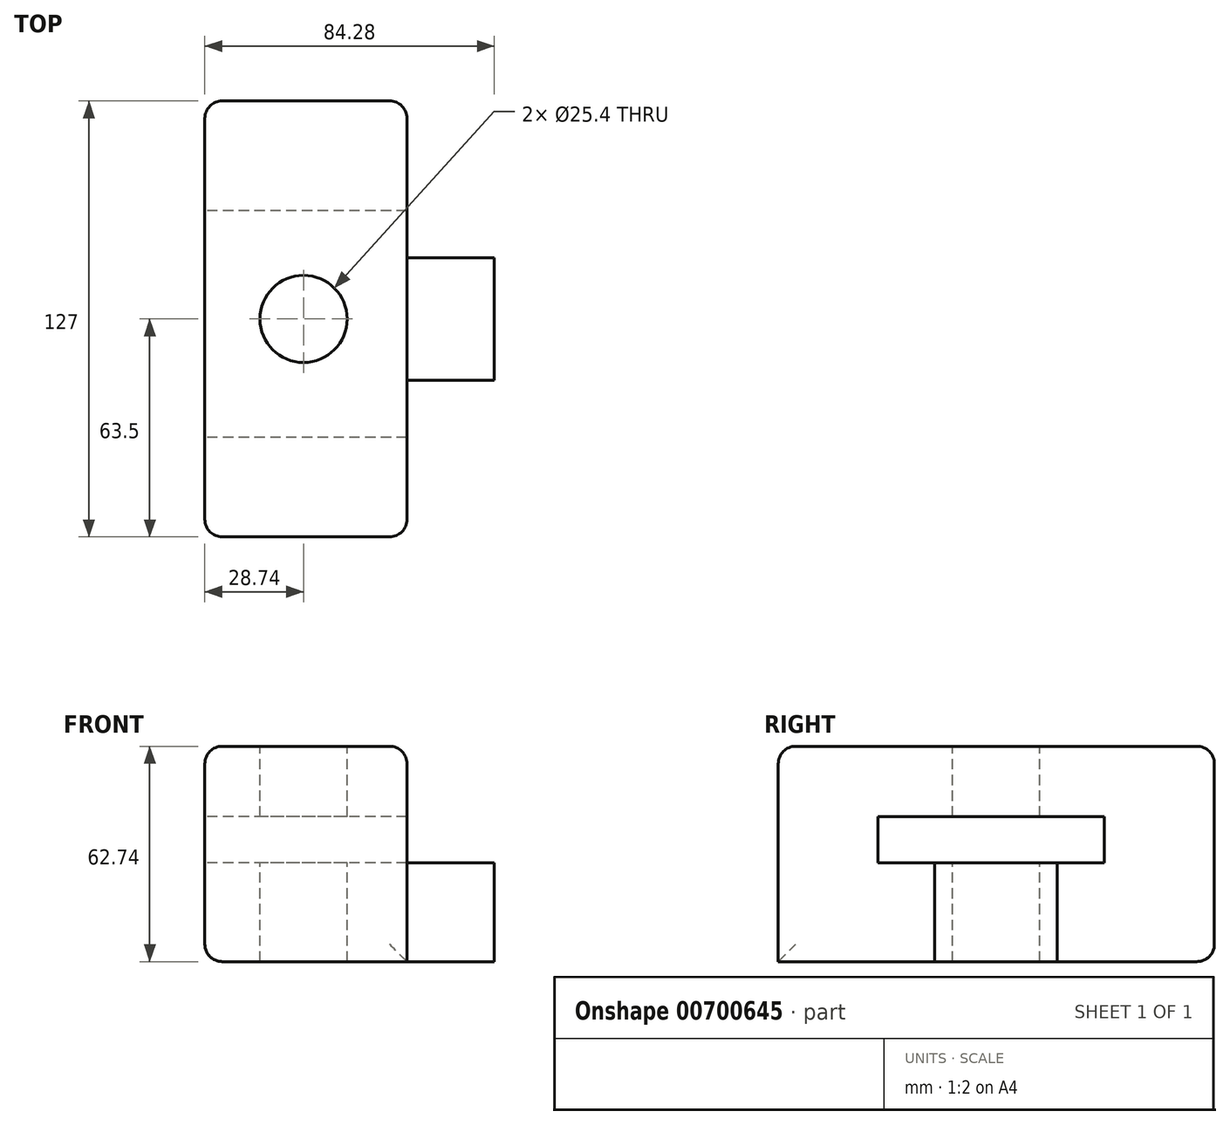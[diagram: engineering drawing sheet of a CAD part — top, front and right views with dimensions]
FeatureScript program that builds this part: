
annotation { "Feature Type Name" : "Feature", "Feature Type Description" : "" }
export const myFeature = defineFeature(function(context is Context, id is Id, definition is map)
    precondition{}
    {
        {
            var Q0;
            Q0=qCreatedBy(makeId("Front.planeOp"),FACE);
            var sketch = newSketch(context, id + "F0", { "sketchPlane" : qUnion([Q0])});
            skLineSegment(sketch, "E0.bottom", {"start": v(-28.74, 34) * mm, "end": v(30.14, 34) * mm});
            skLineSegment(sketch, "E0.top", {"start": v(-28.74, -28.73) * mm, "end": v(30.14, -28.73) * mm});
            skLineSegment(sketch, "E0.left", {"start": v(-28.74, 34) * mm, "end": v(-28.74, -28.73) * mm});
            skLineSegment(sketch, "E0.right", {"start": v(30.14, 34) * mm, "end": v(30.14, -28.73) * mm});
            skSolve(sketch);
        }
        {
            var Q0;
            Q0=makeQuery(id+"F0.imprint","IMPRINT",FACE,{"disambiguationData":[TD([[makeQuery(id+"F0.imprint","IMPRINT",EDGE,{"derivedFrom":sQuery(id+"F0.wireOp",EDGE,"E0.bottom")}),-1.0]])]});
            extrude(context, id + "F1", {"entities" : qUnion([Q0]), "endBound" : BoundingType.SYMMETRIC, "depth" : 127 * mm, "offsetDistance" : 25.4 * mm});
        }
        {
            var Q0;
            Q0=qCreatedBy(makeId("Right.planeOp"),FACE);
            var sketch = newSketch(context, id + "F2", { "sketchPlane" : qUnion([Q0])});
            skLineSegment(sketch, "E1.bottom", {"start": v(-34.45, 13.5) * mm, "end": v(31.48, 13.5) * mm});
            skLineSegment(sketch, "E1.top", {"start": v(-34.45, 0) * mm, "end": v(31.48, 0) * mm});
            skLineSegment(sketch, "E1.left", {"start": v(-34.45, 13.5) * mm, "end": v(-34.45, 0) * mm});
            skLineSegment(sketch, "E1.right", {"start": v(31.48, 13.5) * mm, "end": v(31.48, 0) * mm});
            skSolve(sketch);
        }
        {
            var Q0;
            Q0 = qSketchRegion(id + "F2", true);
            extrude(context, id + "F3", {"entities" : qUnion([Q0]), "operationType" : NewBodyOperationType.REMOVE, "endBound" : BoundingType.THROUGH_ALL, "depth" : 25.4 * mm, "offsetDistance" : 25.4 * mm, "hasSecondDirection" : true, "secondDirectionBound" : SecondDirectionBoundingType.UP_TO_NEXT, "secondDirectionOppositeDirection" : true, "secondDirectionDepth" : 25.4 * mm});
        }
        {
            var Q0;
            Q0=makeQuery(id+"F1.opExtrude","CAP_EDGE",EDGE,{"disambiguationData":[OSD([sQuery(id+"F0.wireOp",EDGE,"E0.bottom")])],"isStart":true});
            fillet(context, id + "F4", {"entities" : qUnion([Q0]), "radius" : 5.08 * mm, "tangentPropagation" : true, "allowEdgeOverflow" : false});
        }
        {
            var Q0;
            Q0=makeQuery(id+"F1.opExtrude","CAP_EDGE",EDGE,{"disambiguationData":[OSD([sQuery(id+"F0.wireOp",EDGE,"E0.bottom")])],"isStart":false});
            fillet(context, id + "F5", {"entities" : qUnion([Q0]), "radius" : 5.08 * mm, "tangentPropagation" : true, "allowEdgeOverflow" : false});
        }
        {
            var Q0;
            Q0=makeQuery(id+"F1.opExtrude","SWEPT_EDGE",EDGE,{"disambiguationData":[OSD([sQuery(id+"F0.wireOp",EDGE,"E0.top"),sQuery(id+"F0.wireOp",EDGE,"E0.left")])]});
            var Q1;
            Q1=makeQuery(id+"F1.opExtrude","CAP_EDGE",EDGE,{"disambiguationData":[OSD([sQuery(id+"F0.wireOp",EDGE,"E0.left")])],"isStart":false});
            var Q2;
            Q2=makeQuery(id+"F1.opExtrude","CAP_EDGE",EDGE,{"disambiguationData":[OSD([sQuery(id+"F0.wireOp",EDGE,"E0.left")])],"isStart":true});
            var Q3;
            Q3=makeQuery(id+"F1.opExtrude","CAP_EDGE",EDGE,{"disambiguationData":[OSD([sQuery(id+"F0.wireOp",EDGE,"E0.right")])],"isStart":true});
            var Q4;
            Q4=makeQuery(id+"F1.opExtrude","SWEPT_EDGE",EDGE,{"disambiguationData":[OSD([sQuery(id+"F0.wireOp",EDGE,"E0.bottom"),sQuery(id+"F0.wireOp",EDGE,"E0.right")])]});
            var Q5;
            Q5=makeQuery(id+"F1.opExtrude","SWEPT_EDGE",EDGE,{"disambiguationData":[OSD([sQuery(id+"F0.wireOp",EDGE,"E0.bottom"),sQuery(id+"F0.wireOp",EDGE,"E0.left")])]});
            var Q6;
            Q6=makeQuery(id+"F1.opExtrude","CAP_EDGE",EDGE,{"disambiguationData":[OSD([sQuery(id+"F0.wireOp",EDGE,"E0.top")])],"isStart":true});
            fillet(context, id + "F6", {"entities" : qUnion([Q0, Q1, Q2, Q3, Q4, Q5, Q6]), "radius" : 5.08 * mm, "tangentPropagation" : true, "allowEdgeOverflow" : false});
        }
        {
            var Q0;
            Q0=makeQuery(id+"F1.opExtrude","SWEPT_FACE",FACE,{"disambiguationData":[OSD([sQuery(id+"F0.wireOp",EDGE,"E0.right")])]});
            var sketch = newSketch(context, id + "F7", { "sketchPlane" : qUnion([Q0])});
            skLineSegment(sketch, "E2", {"start": v(-17.92, 0) * mm, "end": v(-17.92, -28.73) * mm});
            skLineSegment(sketch, "E3", {"start": v(17.76, 0) * mm, "end": v(17.76, -28.73) * mm});
            skSolve(sketch);
        }
        {
            var Q0;
            {var subQ0=sQuery(id+"F7.wireOp",EDGE,"E2");Q0=makeQuery(id+"F7.imprint","IMPRINT",FACE,{"disambiguationData":[TD([[makeQuery(id+"F7.imprint","IMPRINT",EDGE,{"derivedFrom":subQ0}),1.0]])]});}
            extrude(context, id + "F8", {"entities" : qUnion([Q0]), "operationType" : NewBodyOperationType.ADD, "depth" : 25.4 * mm, "offsetDistance" : 25.4 * mm});
        }
        {
            var Q0;
            Q0=makeQuery(id+"F1.opExtrude","SWEPT_FACE",FACE,{"disambiguationData":[OSD([sQuery(id+"F0.wireOp",EDGE,"E0.bottom")])]});
            var sketch = newSketch(context, id + "F9", { "sketchPlane" : qUnion([Q0])});
            skPoint(sketch, "E4", {"position": v(0, 0) * mm});
            skSolve(sketch);
        }
        {
            var Q0;
            Q0=sQuery(id+"F9.wireOp",VERTEX,"E4");
            var Q1;
            Q1=makeQuery(id+"F1.opExtrude","SWEPT_BODY",BODY,{"disambiguationData":[OSD([sQuery(id+"F0.wireOp",EDGE,"E0.bottom"),sQuery(id+"F0.wireOp",EDGE,"E0.top"),sQuery(id+"F0.wireOp",EDGE,"E0.left"),sQuery(id+"F0.wireOp",EDGE,"E0.right")])]});
            hole(context, id + "F10", {"style" : HoleStyle.SIMPLE, "endStyle" : HoleEndStyle.THROUGH, "holeDiameter" : 25.4 * mm, "majorDiameter" : 6.35 * mm, "isTappedThrough" : true, "tappedDepth" : 12.7 * mm, "tapClearance" : 3, "locations" : qUnion([Q0]), "scope" : qUnion([Q1])});
        }
    });
